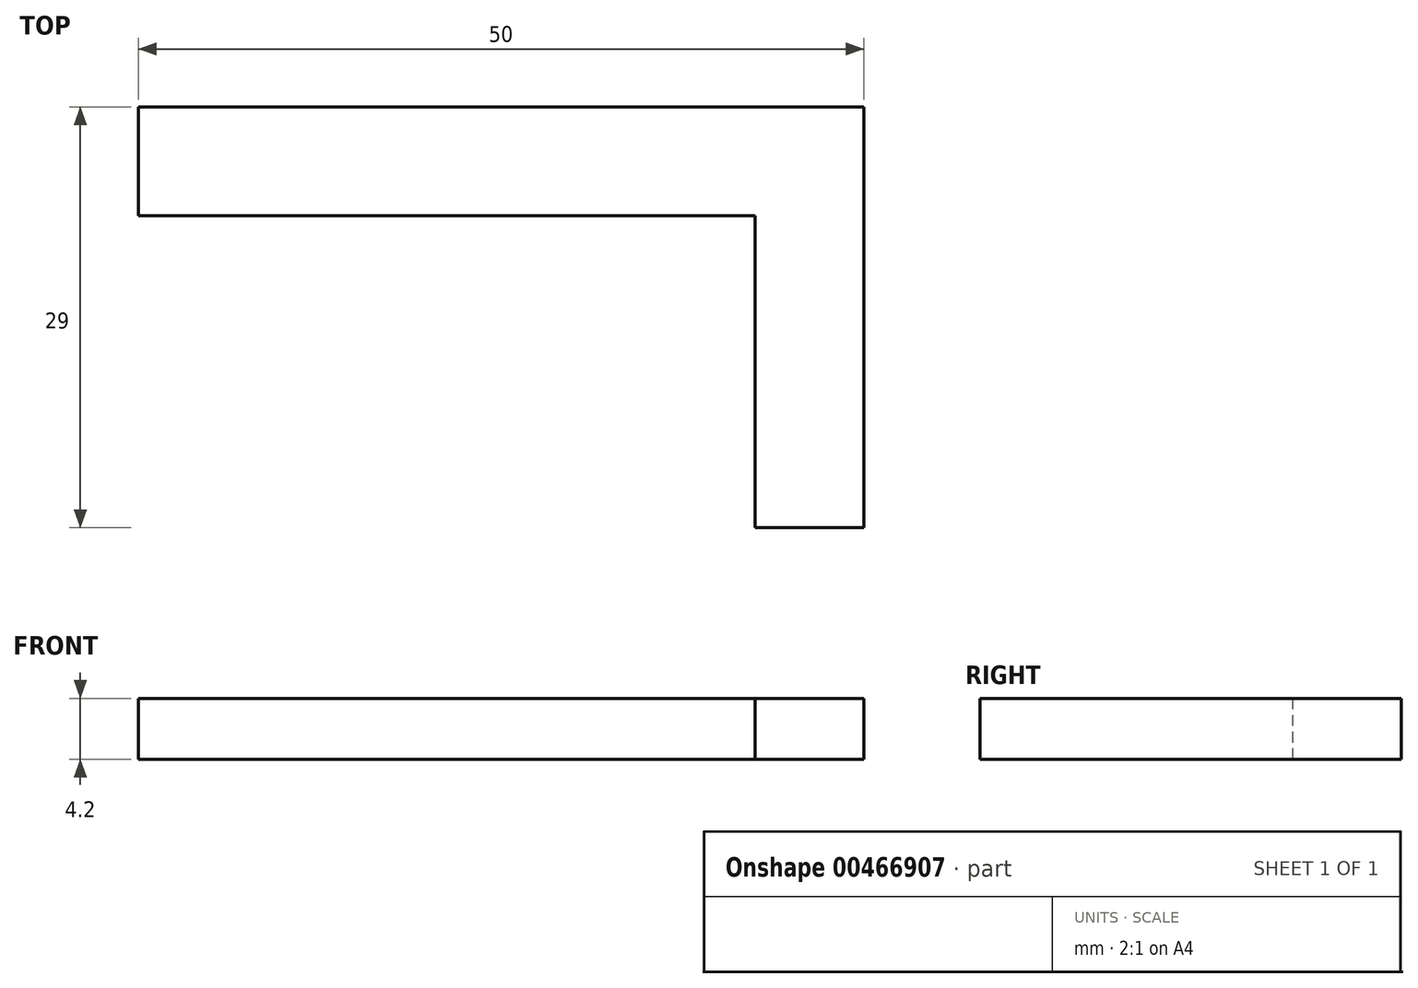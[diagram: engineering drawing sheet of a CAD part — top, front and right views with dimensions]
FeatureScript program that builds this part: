
annotation { "Feature Type Name" : "Feature", "Feature Type Description" : "" }
export const myFeature = defineFeature(function(context is Context, id is Id, definition is map)
    precondition{}
    {
        {
            var Q0;
            Q0=qCreatedBy(makeId("Top.planeOp"),FACE);
            var sketch = newSketch(context, id + "F0", { "sketchPlane" : qUnion([Q0])});
            skLineSegment(sketch, "E0.bottom", {"start": v(-25, -3.75) * mm, "end": v(25, -3.75) * mm});
            skLineSegment(sketch, "E0.top", {"start": v(-25, 3.75) * mm, "end": v(25, 3.75) * mm});
            skLineSegment(sketch, "E0.left", {"start": v(-25, -3.75) * mm, "end": v(-25, 3.75) * mm});
            skLineSegment(sketch, "E0.right", {"start": v(25, -3.75) * mm, "end": v(25, 3.75) * mm});
            skPoint(sketch, "E0.middle", {"position": v(0, 0) * mm});
            skLineSegment(sketch, "E1.bottom", {"start": v(25, 3.75) * mm, "end": v(17.5, 3.75) * mm});
            skLineSegment(sketch, "E1.top", {"start": v(25, -25.25) * mm, "end": v(17.5, -25.25) * mm});
            skLineSegment(sketch, "E1.left", {"start": v(25, 3.75) * mm, "end": v(25, -25.25) * mm});
            skLineSegment(sketch, "E1.right", {"start": v(17.5, 3.75) * mm, "end": v(17.5, -25.25) * mm});
            skSolve(sketch);
        }
        {
            var Q0;
            Q0=qSketchRegion(id+"F0",true);
            extrude(context, id + "F1", {"entities" : qUnion([Q0]), "depth" : 4.2 * mm});
        }
        {
            var Q0;
            Q0=qSketchRegion(id+"F0",true);
            extrude(context, id + "F2", {"entities" : qUnion([Q0]), "operationType" : NewBodyOperationType.ADD, "depth" : 4.2 * mm});
        }
    });
